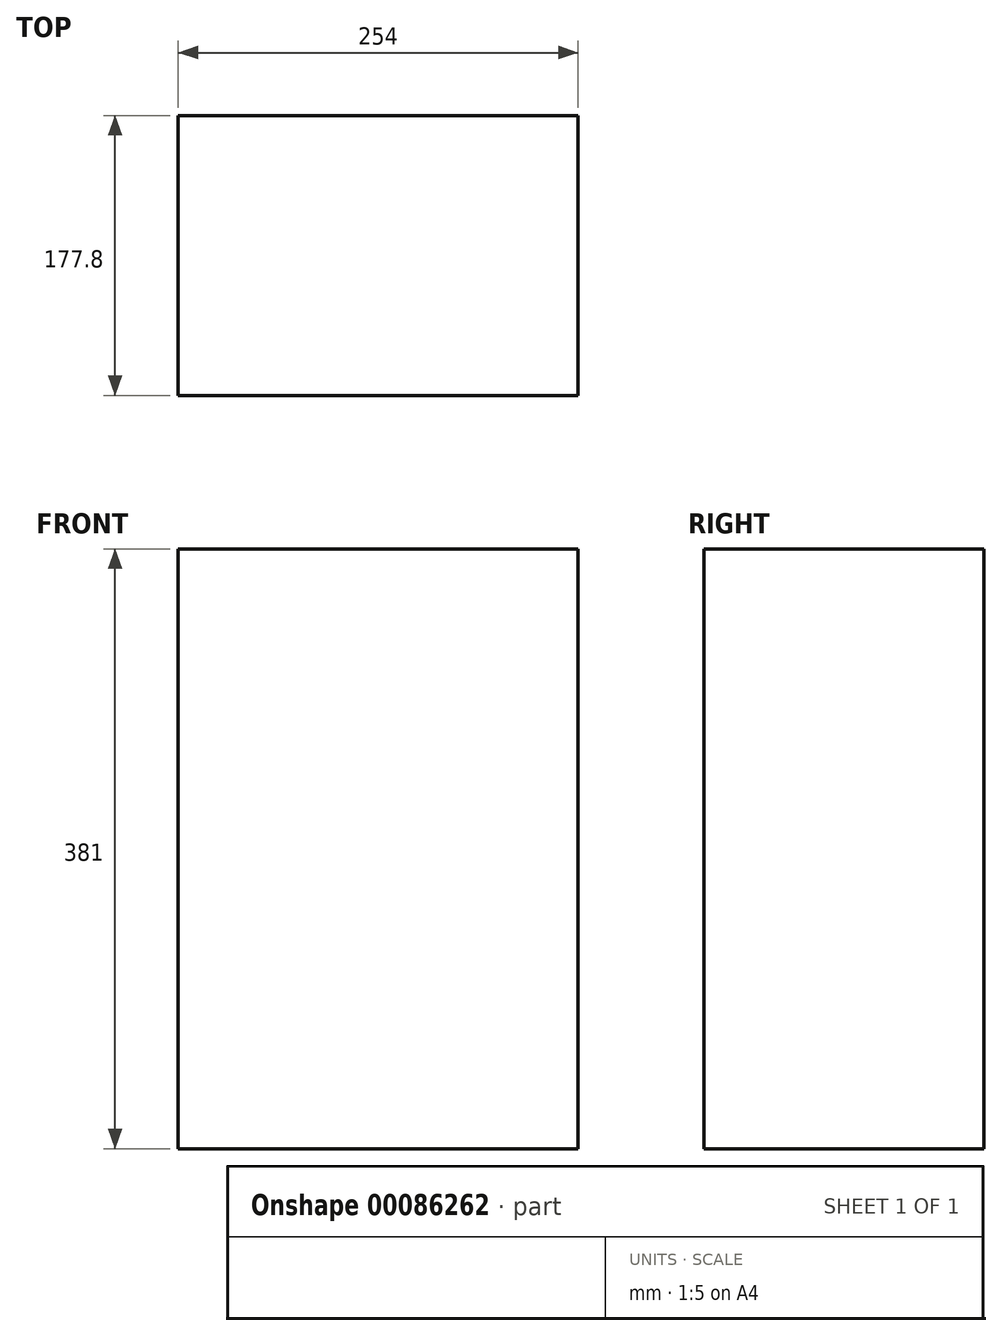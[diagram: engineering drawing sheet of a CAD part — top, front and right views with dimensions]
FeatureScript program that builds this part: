
annotation { "Feature Type Name" : "Feature", "Feature Type Description" : "" }
export const myFeature = defineFeature(function(context is Context, id is Id, definition is map)
    precondition{}
    {
        {
            var Q0;
            Q0=qCreatedBy(makeId("Top.planeOp"),FACE);
            var sketch = newSketch(context, id + "F0", { "sketchPlane" : qUnion([Q0])});
            skLineSegment(sketch, "E0.bottom", {"start": v(127, 88.9) * mm, "end": v(-127, 88.9) * mm});
            skLineSegment(sketch, "E0.top", {"start": v(127, -88.9) * mm, "end": v(-127, -88.9) * mm});
            skLineSegment(sketch, "E0.left", {"start": v(127, 88.9) * mm, "end": v(127, -88.9) * mm});
            skLineSegment(sketch, "E0.right", {"start": v(-127, 88.9) * mm, "end": v(-127, -88.9) * mm});
            skPoint(sketch, "E0.middle", {"position": v(0, 0) * mm});
            skSolve(sketch);
        }
        {
            var Q0;
            Q0=makeQuery(id+"F0.imprint","IMPRINT",FACE,{"disambiguationData":[TD([[makeQuery(id+"F0.imprint","IMPRINT",EDGE,{"derivedFrom":sQuery(id+"F0.wireOp",EDGE,"E0.bottom")}),1.0]])]});
            extrude(context, id + "F1", {"entities" : qUnion([Q0]), "depth" : 381 * mm});
        }
    });
